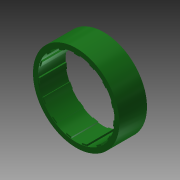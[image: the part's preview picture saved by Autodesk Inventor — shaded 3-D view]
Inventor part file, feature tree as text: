
AUTODESK INVENTOR PART (.ipt)
format: ipt  version: 2015 (Build 190159000, 159)  size: 147,456 bytes
history: native  units: in
note: dims shown in document units (in); Inventor stores cm internally (conversion verified against a paired STEP export)
features: extrude x2, sketch x1, pattern_circular x1
ambient origin geometry x8: Origin, YZ Plane, XZ Plane, XY Plane, X Axis, Y Axis, Z Axis, Center Point
bodies: Body1 (feature_tree)
feature tree (4):
  sketch  "Sketch1"  dims[d0=1.52in d3=0.03in d4=0.1in d7=0.57in d8=0.0in d9=0.55in d10=0.0in d11=5.9055in d12=360.0deg]
  extrude  "Extrusion2"  Depth=0.55in
  extrude  "Extrusion3"  Depth=0.55in
  pattern_circular  "Circular Pattern1"  [2 undecoded]
note: 2 required parameter values undecoded (feature->parameter linkage not recoverable at this tier; creation-order binding heuristic only, values carry confidence <= 0.55)
